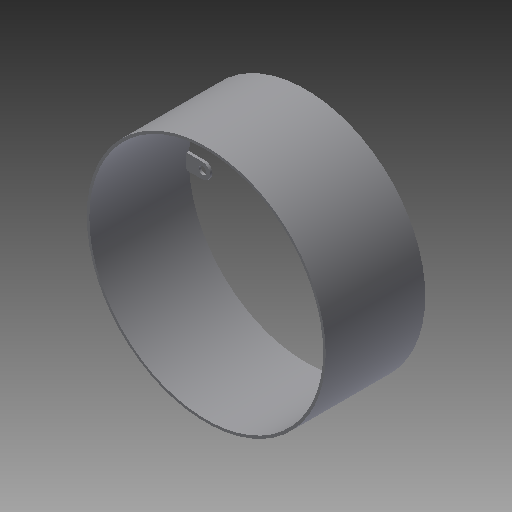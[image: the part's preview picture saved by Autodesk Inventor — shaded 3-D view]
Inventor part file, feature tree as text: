
AUTODESK INVENTOR PART (.ipt)
format: ipt  version: 2017 (Build 210142000, 142)  size: 122,880 bytes
history: native  units: mm
features: extrude x2, sketch x2
ambient origin geometry x8: Origin, YZ Plane, XZ Plane, XY Plane, X Axis, Y Axis, Z Axis, Center Point
bodies: Solid1 (feature_tree)
feature tree (4):
  extrude  "Extrusion1"  Depth=1.0mm
  extrude  "Extrusion2"  [1 undecoded]
  sketch  "Sketch1"  dims[d3=1.0mm d4=0.0mm d5=1.0mm]
  sketch  "Sketch2"  dims[d6=38.0mm d7=0.0mm]
note: 1 required parameter value undecoded (feature->parameter linkage not recoverable at this tier; creation-order binding heuristic only, values carry confidence <= 0.55)
